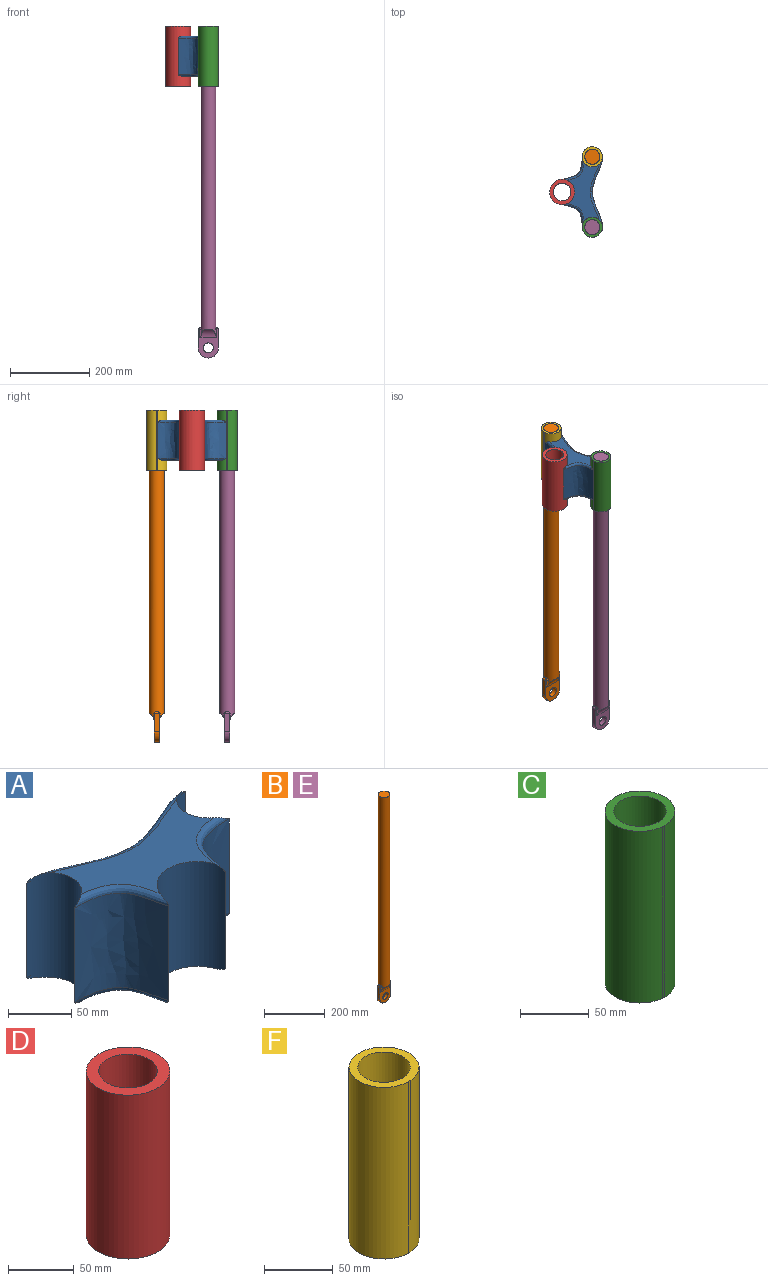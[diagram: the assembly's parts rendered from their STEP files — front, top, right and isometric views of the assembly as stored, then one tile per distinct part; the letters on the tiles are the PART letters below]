
ASSEMBLY  parts=6 mates=6
PART A: 17 faces, bbox 180.4x103x101.6 mm
  f0: cylinder r=25.4mm len=101.6mm, axis (0,0,-1), area 7695.7mm2, adj f1,f6,f7,f8,f10,f12,f14,f16
  f1: extruded ~91.44x88.9mm, area 8532.3mm2, adj f0,f2,f10,f14
  f2: extruded ~91.44x88.9mm, area 8532.3mm2, adj f1,f3,f11,f15
  f3: cylinder r=25.4mm len=101.6mm, axis (0,0,-1), area 7695.7mm2, adj f2,f4,f7,f8,f9,f11,f13,f15
  f4: extruded ~91.44x54.79mm, area 7858.2mm2, adj f3,f5,f9,f13
  f5: cylinder r=31.75mm len=101.6mm, axis (0,0,-1), area 10011.9mm2, adj f4,f6,f7,f8,f9,f12,f13,f16
  f6: extruded ~91.44x54.79mm, area 7858.2mm2, adj f0,f5,f12,f16
  f7: plane 147.85x82.4mm, normal (0,0,1), area 5772.1mm2, adj f0,f3,f5,f13,f14,f15,f16
  f8: plane 147.85x82.4mm, normal (0,0,-1), area 5772.1mm2, adj f0,f3,f5,f9,f10,f11,f12
  f9: bspline ~60.96x57.2mm, area 611.8mm2, adj f3,f4,f5,f8
  f10: bspline ~92.45x30.75mm, area 667mm2, adj f0,f1,f8,f11
  f11: bspline ~92.45x30.75mm, area 667mm2, adj f2,f3,f8,f10
  f12: bspline ~60.96x57.2mm, area 611.8mm2, adj f0,f5,f6,f8
  f13: bspline ~60.96x57.2mm, area 611.8mm2, adj f3,f4,f5,f7
  f14: bspline ~92.45x30.75mm, area 667mm2, adj f0,f1,f7,f15
  f15: bspline ~92.45x30.75mm, area 667mm2, adj f2,f3,f7,f14
  f16: bspline ~60.96x57.2mm, area 611.8mm2, adj f0,f5,f6,f7
PART B: 26 faces, bbox 50.8x38.1x838.2 mm
  f0: cylinder r=19.05mm len=776.06mm, axis (0,0,-1), area 91777.5mm2, adj f1,f2,f7,f8,f9,f10,f11,f12
  f1: plane 38.1x38.1mm, normal (0,0,1), area 1140.1mm2, adj f0
  f2: plane 3.05x1.33mm, normal (0,0,1), area 3.6mm2, adj f0,f20,f22,f24
  f3: plane 45.72x12.7mm, normal (1,0,0), area 580.6mm2, adj f4,f6,f14,f17
  f4: plane 71.12x50.8mm, normal (0,-1,0), area 1965.6mm2, adj f3,f5,f8,f9,f10,f14,f15,f21
  f5: plane 45.72x12.7mm, normal (-1,0,0), area 580.6mm2, adj f4,f6,f14,f22
  f6: plane 71.12x50.8mm, normal (0,1,0), area 1965.6mm2, adj f3,f5,f11,f12,f13,f14,f19,f23
  f7: plane 3.05x1.33mm, normal (0,0,1), area 3.6mm2, adj f0,f16,f17,f18
  f8: cylinder r=25.4mm len=42.5mm, axis (1,0,0), area 815.4mm2, adj f0,f4,f9,f10
  f9: cylinder r=5.08mm len=20.32mm, axis (0,0,-1), area 79mm2, adj f0,f4,f8,f20
  f10: cylinder r=5.08mm len=20.32mm, axis (0,0,-1), area 79mm2, adj f0,f4,f8,f16
  f11: cylinder r=25.4mm len=42.5mm, axis (-1,0,0), area 815.4mm2, adj f0,f6,f12,f13
  f12: cylinder r=5.08mm len=20.32mm, axis (0,0,-1), area 79mm2, adj f0,f6,f11,f24
  f13: cylinder r=5.08mm len=20.32mm, axis (0,0,-1), area 79mm2, adj f0,f6,f11,f18
  f14: cylinder r=25.4mm len=50.8mm, axis (0,-1,0), area 1013.4mm2, adj f3,f4,f5,f6
  f15: cylinder r=5.08mm len=4.99mm, axis (1,0,0), area 18.8mm2, adj f4,f16,f17
  f16: torus R=10.16mm, axis (0,0,-1), area 26.6mm2, adj f0,f7,f10,f15,f17
  f17: cylinder r=5.08mm len=12.7mm, axis (0,-1,0), area 71.9mm2, adj f3,f7,f15,f16,f18,f19
  f18: torus R=10.16mm, axis (0,0,-1), area 26.6mm2, adj f0,f7,f13,f17,f19
  f19: cylinder r=5.08mm len=4.99mm, axis (1,0,0), area 18.8mm2, adj f6,f17,f18
  f20: torus R=10.16mm, axis (0,0,-1), area 26.6mm2, adj f0,f2,f9,f21,f22
  f21: cylinder r=5.08mm len=4.99mm, axis (1,0,0), area 18.8mm2, adj f4,f20,f22
  f22: cylinder r=5.08mm len=12.7mm, axis (0,1,0), area 71.9mm2, adj f2,f5,f20,f21,f23,f24
  f23: cylinder r=5.08mm len=4.99mm, axis (1,0,0), area 18.8mm2, adj f6,f22,f24
  f24: torus R=10.16mm, axis (0,0,-1), area 26.6mm2, adj f0,f2,f12,f22,f23
  f25: cylinder r=12.7mm len=25.4mm, axis (0,1,0), area 1013.4mm2, adj f4,f6
PART C: 7 faces, bbox 50.8x50.8x152.4 mm
  f0: extruded ~152.4x9.97mm, area 1555.6mm2, adj f1,f3,f4,f5
  f1: cylinder r=25.4mm len=152.4mm, axis (0,0,-1), area 10239.4mm2, adj f0,f2,f4,f5
  f2: extruded ~152.4x2.36mm, area 360.7mm2, adj f1,f3,f4,f5
  f3: cylinder r=25.4mm len=152.4mm, axis (0,0,-1), area 12161mm2, adj f0,f2,f4,f5
  f4: plane 50.8x50.8mm, normal (0,0,1), area 885.6mm2, adj f0,f1,f2,f3,f6
  f5: plane 50.8x50.8mm, normal (0,0,-1), area 885.6mm2, adj f0,f1,f2,f3,f6
  f6: cylinder r=19.05mm len=152.4mm, axis (0,0,1), area 18241.5mm2, adj f4,f5
PART D: 4 faces, bbox 63.5x63.5x152.4 mm
  f0: cylinder r=31.75mm len=152.4mm, axis (0,0,-1), area 30402.4mm2, adj f1,f2
  f1: plane 63.5x63.5mm, normal (0,0,1), area 1615.1mm2, adj f0,f3
  f2: plane 63.5x63.5mm, normal (0,0,-1), area 1615.1mm2, adj f0,f3
  f3: cylinder r=22.23mm len=152.4mm, axis (0,0,1), area 21281.7mm2, adj f1,f2
PART E: same geometry as B
PART F: 5 faces, bbox 50.8x50.8x152.4 mm
  f0: extruded ~152.4x2.36mm, area 360.7mm2, adj f1,f2,f3
  f1: cylinder r=25.4mm len=152.4mm, axis (0,0,-1), area 23961.1mm2, adj f0,f2,f3
  f2: plane 50.8x50.8mm, normal (0,0,1), area 886.7mm2, adj f0,f1,f4
  f3: plane 50.8x50.8mm, normal (0,0,-1), area 886.7mm2, adj f0,f1,f4
  f4: cylinder r=19.05mm len=152.4mm, axis (0,0,1), area 18241.5mm2, adj f2,f3
PLACE A rot(axis=(0,0,-1),90deg) t=(36.56,168.82,21.2)mm
PLACE B t=(36.56,257.72,-283.6)mm
PLACE C rot(axis=(0,0,-1),90deg) t=(36.56,168.82,21.2)mm
PLACE D rot(axis=(0,0,-1),90deg) t=(36.56,168.82,21.2)mm
PLACE E t=(36.56,79.92,-283.6)mm
PLACE F rot(axis=(0,0,-1),90deg) t=(36.56,168.82,21.2)mm
MATE revolute F.f4 <-> A.f3  axis (0,0,1) through (36.56,257.72,97.4)mm
MATE revolute E.f0 <-> C.f6  axis (0,0,1) through (36.56,79.92,97.4)mm
MATE revolute B.f0 <-> F.f4  axis (0,0,1) through (36.56,257.72,97.4)mm
MATE revolute D.f0 <-> A.f5  axis (0,0,1) through (-39.64,168.82,97.4)mm
MATE cylindrical B.f14 <-> E.f14  axis (0,-1,0) through (36.56,251.37,-715.4)mm
MATE revolute C.f6 <-> A.f0  axis (0,0,1) through (36.56,79.92,97.4)mm
